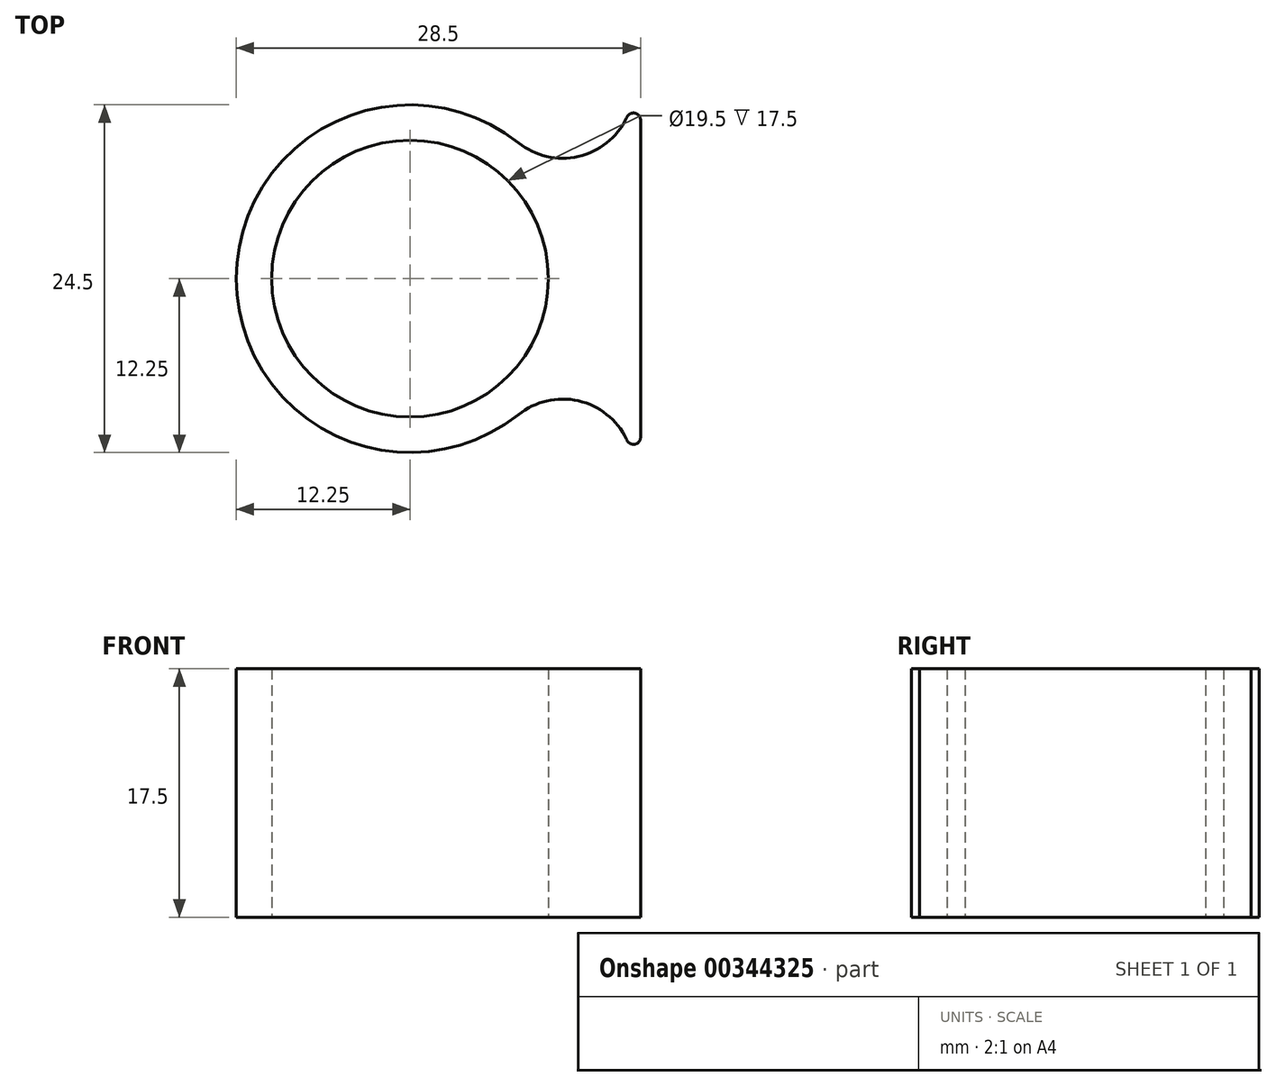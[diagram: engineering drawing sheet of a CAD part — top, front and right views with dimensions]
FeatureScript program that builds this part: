
annotation { "Feature Type Name" : "Feature", "Feature Type Description" : "" }
export const myFeature = defineFeature(function(context is Context, id is Id, definition is map)
    precondition{}
    {
        {
            var Q0;
            Q0=qCreatedBy(makeId("Top.planeOp"),FACE);
            var sketch = newSketch(context, id + "F0", { "sketchPlane" : qUnion([Q0])});
            skCircle(sketch, "E0", {"center": v(0, 0) * mm, "radius": 9.75 * mm});
            skArc(sketch, "E1", {"start": v(11.63, 3.86) * mm, "mid": v(-12.25, 0) * mm, "end": v(11.63, -3.86) * mm});
            skLineSegment(sketch, "E2", {"start": v(16.25, 13.35) * mm, "end": v(16.25, -13.35) * mm});
            skLineSegment(sketch, "E3", {"start": v(16.25, -13.35) * mm, "end": v(11.63, -3.86) * mm});
            skLineSegment(sketch, "E4", {"start": v(11.63, 3.86) * mm, "end": v(16.25, 13.35) * mm});
            skPoint(sketch, "E5.orphan", {"position": v(9.75, 0) * mm});
            skSolve(sketch);
        }
        {
            var Q0;
            Q0=makeQuery(id+"F0.imprint","IMPRINT",FACE,{"disambiguationData":[TD([[makeQuery(id+"F0.imprint","IMPRINT",EDGE,{"derivedFrom":sQuery(id+"F0.wireOp",EDGE,"E0")}),-1.0]])]});
            extrude(context, id + "F1", {"entities" : qUnion([Q0]), "depth" : 17.5 * mm});
        }
        {
            var Q0;
            Q0=makeQuery(id+"F1.opExtrude","SWEPT_EDGE",EDGE,{"disambiguationData":[OSD([sQuery(id+"F0.wireOp",EDGE,"E1"),sQuery(id+"F0.wireOp",EDGE,"E3")])]});
            var Q1;
            Q1=makeQuery(id+"F1.opExtrude","SWEPT_EDGE",EDGE,{"disambiguationData":[OSD([sQuery(id+"F0.wireOp",EDGE,"E1"),sQuery(id+"F0.wireOp",EDGE,"E4")])]});
            fillet(context, id + "F2", {"entities" : qUnion([Q0, Q1]), "radius" : 5 * mm, "tangentPropagation" : true, "allowEdgeOverflow" : false});
        }
        {
            var Q0;
            Q0=makeQuery(id+"F1.opExtrude","SWEPT_EDGE",EDGE,{"disambiguationData":[OSD([sQuery(id+"F0.wireOp",EDGE,"E2"),sQuery(id+"F0.wireOp",EDGE,"E4")])]});
            var Q1;
            Q1=makeQuery(id+"F1.opExtrude","SWEPT_EDGE",EDGE,{"disambiguationData":[OSD([sQuery(id+"F0.wireOp",EDGE,"E2"),sQuery(id+"F0.wireOp",EDGE,"E3")])]});
            fillet(context, id + "F3", {"entities" : qUnion([Q0, Q1]), "radius" : 0.5 * mm, "tangentPropagation" : true, "allowEdgeOverflow" : false});
        }
    });
